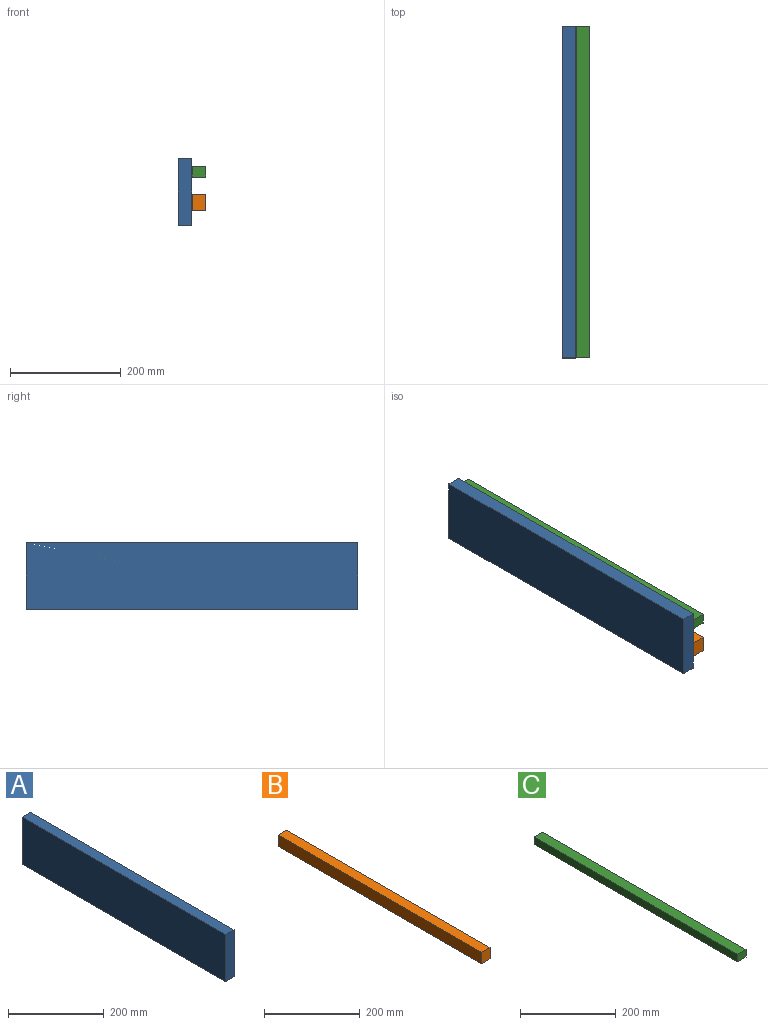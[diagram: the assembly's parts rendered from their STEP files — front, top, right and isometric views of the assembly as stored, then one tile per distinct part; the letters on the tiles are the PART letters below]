
ASSEMBLY  parts=3 mates=2
PART A: 6 faces, bbox 25x600x120 mm
  f0: plane 600x120mm, normal (1,0,0), area 72000mm2, adj f1,f3,f4,f5
  f1: plane 600x25mm, normal (0,0,1), area 15000mm2, adj f0,f2,f4,f5
  f2: plane 600x120mm, normal (-1,0,0), area 72000mm2, adj f1,f3,f4,f5
  f3: plane 600x25mm, normal (0,0,-1), area 15000mm2, adj f0,f2,f4,f5
  f4: plane 120x25mm, normal (0,-1,0), area 3000mm2, adj f0,f1,f2,f3
  f5: plane 120x25mm, normal (0,1,0), area 3000mm2, adj f0,f1,f2,f3
PART B: 6 faces, bbox 25x600x29 mm
  f0: plane 600x29mm, normal (1,0,0), area 17400mm2, adj f1,f3,f4,f5
  f1: plane 600x25mm, normal (0,0,1), area 15000mm2, adj f0,f2,f4,f5
  f2: plane 600x29mm, normal (-1,0,0), area 17400mm2, adj f1,f3,f4,f5
  f3: plane 600x25mm, normal (0,0,-1), area 15000mm2, adj f0,f2,f4,f5
  f4: plane 29x25mm, normal (0,-1,0), area 725mm2, adj f0,f1,f2,f3
  f5: plane 29x25mm, normal (0,1,0), area 725mm2, adj f0,f1,f2,f3
PART C: 6 faces, bbox 25x600x19 mm
  f0: plane 600x19mm, normal (1,0,0), area 11400mm2, adj f1,f3,f4,f5
  f1: plane 600x25mm, normal (0,0,1), area 15000mm2, adj f0,f2,f4,f5
  f2: plane 600x19mm, normal (-1,0,0), area 11400mm2, adj f1,f3,f4,f5
  f3: plane 600x25mm, normal (0,0,-1), area 15000mm2, adj f0,f2,f4,f5
  f4: plane 25x19mm, normal (0,-1,0), area 475mm2, adj f0,f1,f2,f3
  f5: plane 25x19mm, normal (0,1,0), area 475mm2, adj f0,f1,f2,f3
PLACE A t=(175.58,-86.39,86.6)mm
PLACE B t=(25.89,-86.39,87.63)mm
PLACE C t=(103.49,-86.39,148.63)mm
MATE fastened C.f4 <-> A.f4  axis (0,-1,0) through (-533.36,-686.39,-40.85)mm
MATE fastened B.f4 <-> A.f4  axis (0,-1,0) through (-533.36,-686.39,-120.85)mm
